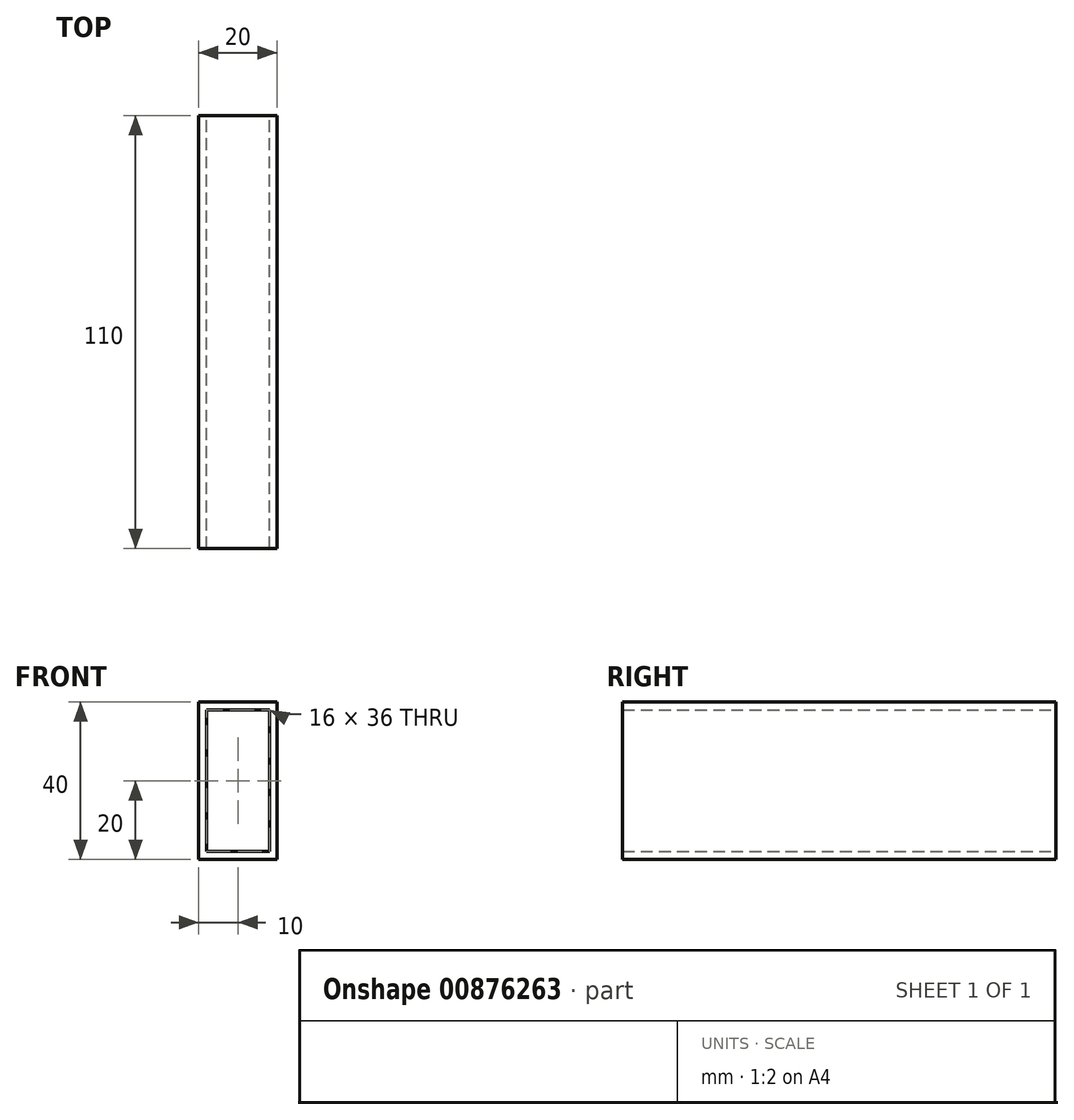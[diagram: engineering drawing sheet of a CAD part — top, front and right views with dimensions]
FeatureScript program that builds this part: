
annotation { "Feature Type Name" : "Feature", "Feature Type Description" : "" }
export const myFeature = defineFeature(function(context is Context, id is Id, definition is map)
    precondition{}
    {
        {
            var Q0;
            Q0=qCreatedBy(makeId("Front.planeOp"),FACE);
            var sketch = newSketch(context, id + "F0", { "sketchPlane" : qUnion([Q0])});
            skLineSegment(sketch, "E0.bottom", {"start": v(0, 0) * mm, "end": v(20, 0) * mm});
            skLineSegment(sketch, "E0.top", {"start": v(0, -40) * mm, "end": v(20, -40) * mm});
            skLineSegment(sketch, "E0.left", {"start": v(0, 0) * mm, "end": v(0, -40) * mm});
            skLineSegment(sketch, "E0.right", {"start": v(20, 0) * mm, "end": v(20, -40) * mm});
            skLineSegment(sketch, "E1.0", {"start": v(2, -2) * mm, "end": v(18, -2) * mm});
            skLineSegment(sketch, "E1.1", {"start": v(2, -2) * mm, "end": v(2, -38) * mm});
            skLineSegment(sketch, "E1.2", {"start": v(2, -38) * mm, "end": v(18, -38) * mm});
            skLineSegment(sketch, "E1.3", {"start": v(18, -2) * mm, "end": v(18, -38) * mm});
            skSolve(sketch);
        }
        {
            var Q0;
            Q0=makeQuery(id+"F0.imprint","IMPRINT",FACE,{"disambiguationData":[TD([[makeQuery(id+"F0.imprint","IMPRINT",EDGE,{"derivedFrom":sQuery(id+"F0.wireOp",EDGE,"E0.bottom")}),-1.0]])]});
            extrude(context, id + "F1", {"entities" : qUnion([Q0]), "depth" : 110 * mm, "offsetDistance" : 25.4 * mm});
        }
    });
